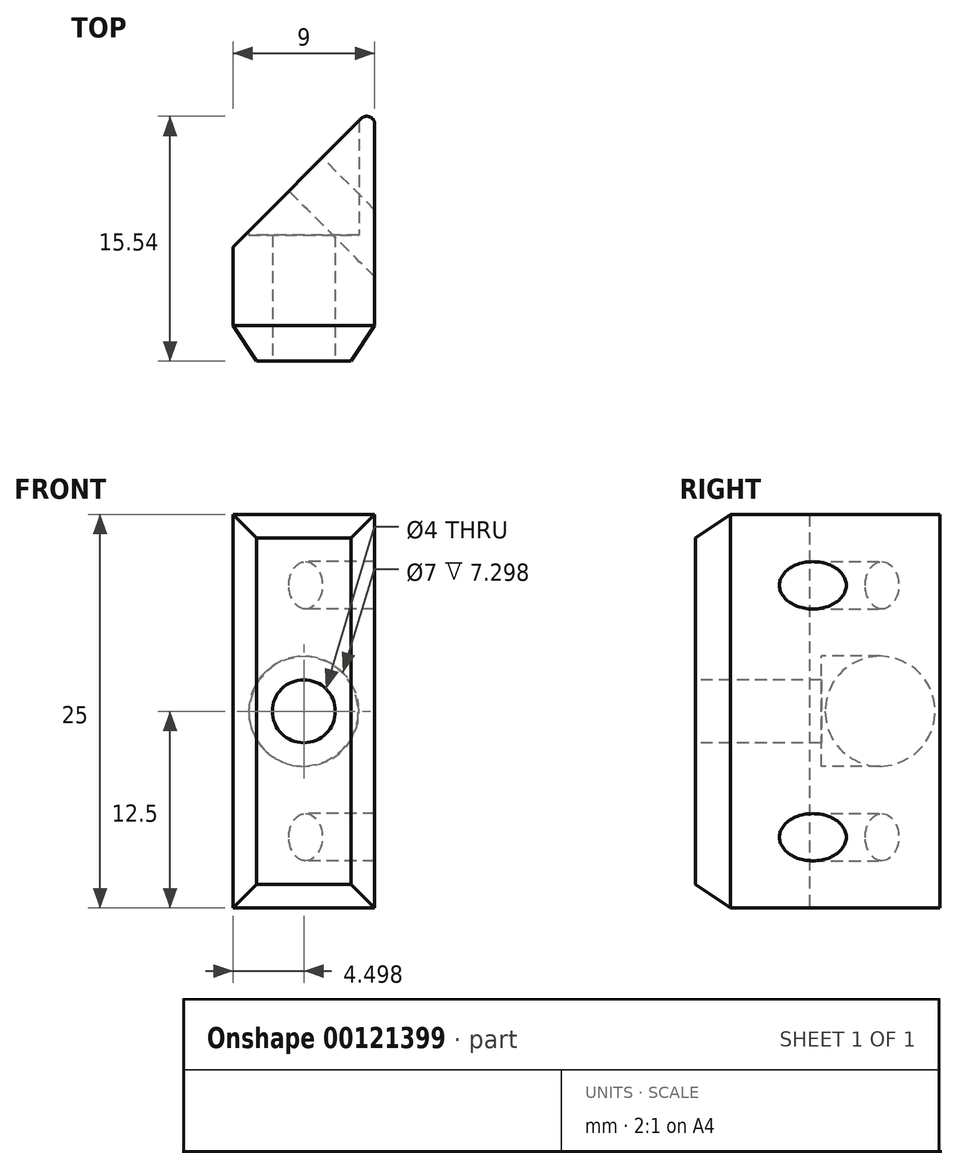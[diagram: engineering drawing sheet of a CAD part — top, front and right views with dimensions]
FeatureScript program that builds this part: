
annotation { "Feature Type Name" : "Feature", "Feature Type Description" : "" }
export const myFeature = defineFeature(function(context is Context, id is Id, definition is map)
    precondition{}
    {
        {
            var Q0;
            Q0=qCreatedBy(makeId("Top.planeOp"),FACE);
            var sketch = newSketch(context, id + "F0", { "sketchPlane" : qUnion([Q0])});
            skLineSegment(sketch, "E0", {"start": v(2.7, 8.75) * mm, "end": v(2.7, 16.54) * mm});
            skLineSegment(sketch, "E1", {"start": v(1.85, 16.9) * mm, "end": v(-6.3, 8.75) * mm});
            skPoint(sketch, "E2.visualSharp", {"position": v(2.7, 17.75) * mm});
            skArc(sketch, "E2.filletArc", {"start": v(2.7, 16.54) * mm, "mid": v(2.4, 17) * mm, "end": v(1.85, 16.9) * mm});
            skLineSegment(sketch, "E3.0", {"start": v(-4.8, 1.5) * mm, "end": v(1.2, 1.5) * mm});
            skLineSegment(sketch, "E4", {"start": v(-6.3, 8.75) * mm, "end": v(-6.3, 3.75) * mm});
            skLineSegment(sketch, "E5", {"start": v(2.7, 8.75) * mm, "end": v(2.7, 3.75) * mm});
            skLineSegment(sketch, "E6", {"start": v(2.7, 3.75) * mm, "end": v(1.2, 1.5) * mm});
            skLineSegment(sketch, "E7", {"start": v(-6.3, 3.75) * mm, "end": v(-4.8, 1.5) * mm});
            skSolve(sketch);
        }
        {
            var Q0;
            Q0 = qSketchRegion(id + "F0", true);
            extrude(context, id + "F1", {"entities" : qUnion([Q0]), "depth" : 25 * mm});
        }
        {
            var Q0;
            Q0=makeQuery(id+"F1.opExtrude","CAP_EDGE",EDGE,{"disambiguationData":[OSD([sQuery(id+"F0.wireOp",EDGE,"pwgyQR9C-kkAf-Ldzy-Lflk-BIyTJrdxJifW")])],"isStart":false});
            var Q1;
            Q1=makeQuery(id+"F1.opExtrude","CAP_EDGE",EDGE,{"disambiguationData":[OSD([sQuery(id+"F0.wireOp",EDGE,"pwgyQR9C-kkAf-Ldzy-Lflk-BIyTJrdxJifW")])],"isStart":true});
            var Q2;
            Q2=makeQuery(id+"F1.opExtrude","CAP_EDGE",EDGE,{"disambiguationData":[OSD([sQuery(id+"F0.wireOp",EDGE,"E3.0")])],"isStart":false});
            var Q3;
            Q3=makeQuery(id+"F1.opExtrude","CAP_EDGE",EDGE,{"disambiguationData":[OSD([sQuery(id+"F0.wireOp",EDGE,"E3.0")])],"isStart":true});
            chamfer(context, id + "F2", {"entities" : qUnion([Q0, Q1, Q2, Q3]), "chamferType" : ChamferType.TWO_OFFSETS, "width1" : 1.5 * mm, "oppositeDirection" : true, "width2" : 2.25 * mm, "tangentPropagation" : true});
        }
        {
            var Q0;
            Q0=makeQuery(id+"F1.opExtrude","SWEPT_FACE",FACE,{"disambiguationData":[OSD([sQuery(id+"F0.wireOp",EDGE,"E3.0")])]});
            var sketch = newSketch(context, id + "F3", { "sketchPlane" : qUnion([Q0])});
            skLineSegment(sketch, "E8.0.0", {"start": v(-4.8, 23.5) * mm, "end": v(-4.8, 1.5) * mm});
            skLineSegment(sketch, "E8.0.1", {"start": v(-4.8, 1.5) * mm, "end": v(1.2, 1.5) * mm});
            skLineSegment(sketch, "E8.0.2", {"start": v(1.2, 1.5) * mm, "end": v(1.2, 23.5) * mm});
            skLineSegment(sketch, "E8.0.3", {"start": v(1.2, 23.5) * mm, "end": v(-4.8, 23.5) * mm});
            skLineSegment(sketch, "E9", {"start": v(1.2, 23.5) * mm, "end": v(-4.8, 1.5) * mm});
            skLineSegment(sketch, "E10", {"start": v(1.2, 1.5) * mm, "end": v(-4.8, 23.5) * mm});
            skPoint(sketch, "E11", {"position": v(-1.8, 12.5) * mm});
            skSolve(sketch);
        }
        {
            var Q0;
            Q0=sQuery(id+"F3.wireOp",VERTEX,"E11");
            var Q1;
            Q1=makeQuery(id+"F1.opExtrude","SWEPT_BODY",BODY,{"disambiguationData":[OSD([sQuery(id+"F0.wireOp",EDGE,"znBoxpV9-RQrd-kkiK-O4kv-IIundqMDa7WY"),sQuery(id+"F0.wireOp",EDGE,"5ManuJkR-w8jX-Z3Bt-5Qa9-bP50sJ5AhwDT"),sQuery(id+"F0.wireOp",EDGE,"pwgyQR9C-kkAf-Ldzy-Lflk-BIyTJrdxJifW"),sQuery(id+"F0.wireOp",EDGE,"E0"),sQuery(id+"F0.wireOp",EDGE,"E1"),sQuery(id+"F0.wireOp",EDGE,"E2.filletArc")])]});
            hole(context, id + "F4", {"style" : HoleStyle.SIMPLE, "endStyle" : HoleEndStyle.THROUGH, "holeDiameter" : 4 * mm, "locations" : qUnion([Q0]), "scope" : qUnion([Q1]), "isTappedThrough" : true});
        }
        {
            var Q0;
            Q0=makeQuery(id+"F1.opExtrude","SWEPT_FACE",FACE,{"disambiguationData":[OSD([sQuery(id+"F0.wireOp",EDGE,"E1")])]});
            var sketch = newSketch(context, id + "F5", { "sketchPlane" : qUnion([Q0])});
            skLineSegment(sketch, "E12", {"start": v(-13.26, 12.5) * mm, "end": v(-13.26, 12.5) * mm});
            skLineSegment(sketch, "E13.0", {"start": v(-1.74, 20.5) * mm, "end": v(-13.26, 20.5) * mm, "construction": true});
            skLineSegment(sketch, "E14.0", {"start": v(-1.74, 4.5) * mm, "end": v(-13.26, 4.5) * mm, "construction": true});
            skLineSegment(sketch, "E15.0", {"start": v(-8.26, 15) * mm, "end": v(-8.26, 0) * mm, "construction": true});
            skPoint(sketch, "E16", {"position": v(-8.26, 4.5) * mm});
            skPoint(sketch, "E17", {"position": v(-8.26, 20.5) * mm});
            skSolve(sketch);
        }
        {
            var Q0;
            Q0=sQuery(id+"F5.wireOp",VERTEX,"E16");
            var Q1;
            Q1=sQuery(id+"F5.wireOp",VERTEX,"E17");
            var Q2;
            Q2=makeQuery(id+"F1.opExtrude","SWEPT_BODY",BODY,{"disambiguationData":[OSD([sQuery(id+"F0.wireOp",EDGE,"znBoxpV9-RQrd-kkiK-O4kv-IIundqMDa7WY"),sQuery(id+"F0.wireOp",EDGE,"5ManuJkR-w8jX-Z3Bt-5Qa9-bP50sJ5AhwDT"),sQuery(id+"F0.wireOp",EDGE,"pwgyQR9C-kkAf-Ldzy-Lflk-BIyTJrdxJifW"),sQuery(id+"F0.wireOp",EDGE,"E0"),sQuery(id+"F0.wireOp",EDGE,"E1"),sQuery(id+"F0.wireOp",EDGE,"E2.filletArc")])]});
            hole(context, id + "F6", {"style" : HoleStyle.SIMPLE, "endStyle" : HoleEndStyle.THROUGH, "holeDiameter" : 3 * mm, "locations" : qUnion([Q0, Q1]), "scope" : qUnion([Q2]), "isTappedThrough" : true});
        }
        {
            var Q0;
            Q0=makeQuery(id+"F1.opExtrude","SWEPT_FACE",FACE,{"disambiguationData":[OSD([sQuery(id+"F0.wireOp",EDGE,"E3.0")])]});
            cPlane(context, id + "F7", {"entities" : qUnion([Q0]), "cplaneType" : CPlaneType.OFFSET, "offset" : 8 * mm, "oppositeDirection" : true, "width" : 150 * mm, "height" : 150 * mm});
        }
        {
            var Q0;
            Q0=qCreatedBy(id+"F7.planeOp",FACE);
            var sketch = newSketch(context, id + "F8", { "sketchPlane" : qUnion([Q0])});
            skCircle(sketch, "E18.0", {"center": v(-1.8, 12.5) * mm, "radius": 2 * mm});
            skCircle(sketch, "E19", {"center": v(-1.8, 12.5) * mm, "radius": 3.5 * mm});
            skSolve(sketch);
        }
        {
            var Q0;
            Q0=sQuery(id+"F8.wireOp",VERTEX,"E18.0.center");
            var Q1;
            Q1=makeQuery(id+"F1.opExtrude","SWEPT_BODY",BODY,{"disambiguationData":[OSD([sQuery(id+"F0.wireOp",EDGE,"znBoxpV9-RQrd-kkiK-O4kv-IIundqMDa7WY"),sQuery(id+"F0.wireOp",EDGE,"5ManuJkR-w8jX-Z3Bt-5Qa9-bP50sJ5AhwDT"),sQuery(id+"F0.wireOp",EDGE,"pwgyQR9C-kkAf-Ldzy-Lflk-BIyTJrdxJifW"),sQuery(id+"F0.wireOp",EDGE,"E0"),sQuery(id+"F0.wireOp",EDGE,"E1"),sQuery(id+"F0.wireOp",EDGE,"E2.filletArc")])]});
            hole(context, id + "F9", {"style" : HoleStyle.SIMPLE, "endStyle" : HoleEndStyle.THROUGH, "holeDiameter" : 7 * mm, "locations" : qUnion([Q0]), "scope" : qUnion([Q1]), "isTappedThrough" : true});
        }
    });
